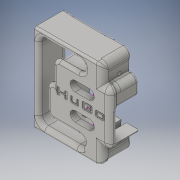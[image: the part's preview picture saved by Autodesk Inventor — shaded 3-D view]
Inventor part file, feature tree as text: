
AUTODESK INVENTOR PART (.ipt)
format: ipt  version: 2016 (Build 200138000, 138)  size: 879,104 bytes
history: native  units: in
note: dims shown in document units (in); Inventor stores cm internally (conversion verified against a paired STEP export)
features: sketch x18, other x3, plane x2
ambient origin geometry x8: Origin, YZ Plane, XZ Plane, XY Plane, X Axis, Y Axis, Z Axis, Center Point
bodies: Solid1 (feature_tree)
feature tree (23):
  other  "Hip_rotation_temp_MIR.ipt"
  other  "Solid1::Hip_rotation_temp_MIR.ipt"
  other  "TaggingFeature1"
  sketch  "Sketch1"  dims[d0=0.3937in]
  sketch  "Sketch12"
  sketch  "Sketch14"
  sketch  "Sketch17"
  sketch  "Sketch18"
  sketch  "Sketch20"
  sketch  "Sketch21"
  sketch  "Sketch22"
  sketch  "Sketch25"
  sketch  "Sketch26"
  sketch  "Sketch27"
  sketch  "Sketch13"
  sketch  "Sketch15"
  sketch  "Sketch16"
  sketch  "Sketch24"
  sketch  "Sketch28"
  sketch  "Sketch29"
  sketch  "Sketch31"
  plane  "Work Plane1"
  plane  "Work Plane2"
